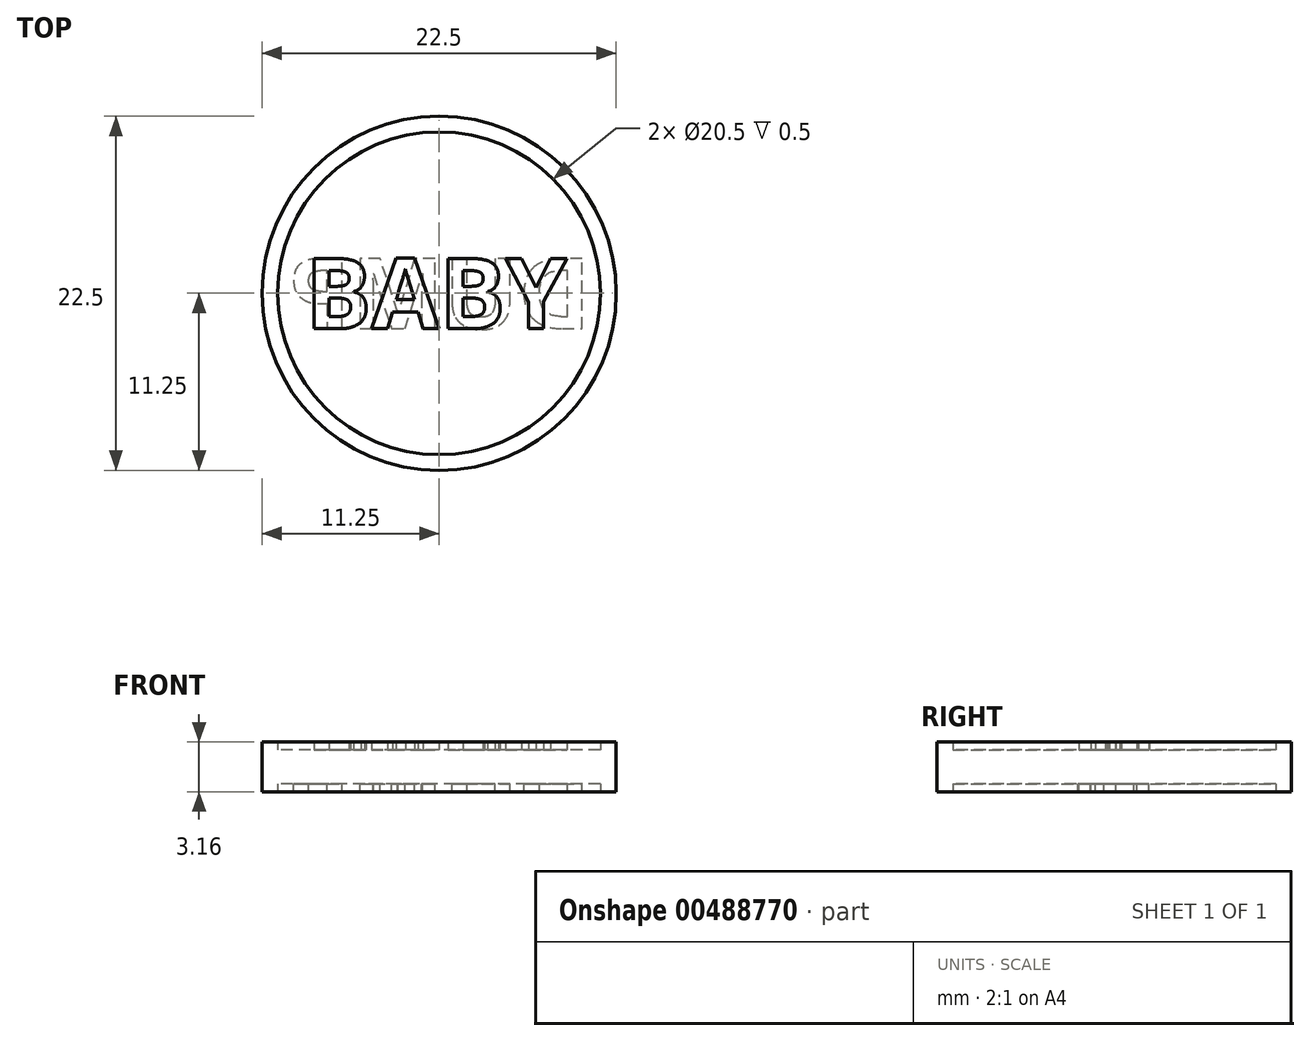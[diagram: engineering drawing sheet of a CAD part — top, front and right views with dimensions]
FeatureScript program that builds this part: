
annotation { "Feature Type Name" : "Feature", "Feature Type Description" : "" }
export const myFeature = defineFeature(function(context is Context, id is Id, definition is map)
    precondition{}
    {
        {
            var Q0;
            Q0=qCreatedBy(makeId("Top.planeOp"),FACE);
            var sketch = newSketch(context, id + "F0", { "sketchPlane" : qUnion([Q0])});
            skCircle(sketch, "E0", {"center": v(0, 0) * mm, "radius": 11.25 * mm});
            skCircle(sketch, "E1", {"center": v(0, 0) * mm, "radius": 10.25 * mm});
            skSolve(sketch);
        }
        {
            var Q0;
            Q0=makeQuery(id+"F0.imprint","IMPRINT",FACE,{"disambiguationData":[TD([[makeQuery(id+"F0.imprint","IMPRINT",EDGE,{"derivedFrom":sQuery(id+"F0.wireOp",EDGE,"E0")}),1.0]])]});
            extrude(context, id + "F1", {"entities" : qUnion([Q0]), "endBound" : BoundingType.SYMMETRIC, "depth" : 3.15 * mm});
        }
        {
            var Q0;
            Q0=qCreatedBy(makeId("Top.planeOp"),FACE);
            var sketch = newSketch(context, id + "F2", { "sketchPlane" : qUnion([Q0])});
            skCircle(sketch, "E2", {"center": v(0, 0) * mm, "radius": 11 * mm});
            skSolve(sketch);
        }
        {
            var Q0;
            Q0 = qSketchRegion(id + "F2", true);
            extrude(context, id + "F3", {"entities" : qUnion([Q0]), "operationType" : NewBodyOperationType.ADD, "endBound" : BoundingType.SYMMETRIC, "depth" : 2.15 * mm});
        }
        {
            var Q0;
            Q0=qCreatedBy(makeId("Top.planeOp"),FACE);
            var sketch = newSketch(context, id + "F4", { "sketchPlane" : qUnion([Q0])});
            skText(sketch, "E3", { "text": "BABY", "fontName": "OpenSans-Bold.ttf"});
            skPoint(sketch, "E4.endSnap0", {"position": v(8.5, 0) * mm});
            skLineSegment(sketch, "E5", {"start": v(-8.5, -2.25) * mm, "end": v(8.5, 2.25) * mm, "construction": true});
            const initialGuessF4  = {"E3": [-0.0085, -0.00225, 1, 0, 0.0045]};
            skSetInitialGuess(sketch, initialGuessF4);
            skSolve(sketch);
        }
        {
            var Q0;
            Q0 = qSketchRegion(id + "F4", true);
            var Q1;
            Q1=makeQuery(id+"F1.opExtrude","CAP_FACE",FACE,{"disambiguationData":[OSD([sQuery(id+"F0.wireOp",EDGE,"E0"),sQuery(id+"F0.wireOp",EDGE,"E1")])],"isStart":false});
            extrude(context, id + "F5", {"entities" : qUnion([Q0]), "operationType" : NewBodyOperationType.ADD, "endBound" : BoundingType.UP_TO_SURFACE, "endBoundEntityFace" : qUnion([Q1]), "depth" : .5 * mm});
        }
        {
            var Q0;
            Q0=makeQuery(id+"F3.opExtrude","CAP_FACE",FACE,{"disambiguationData":[OSD([sQuery(id+"F2.wireOp",EDGE,"E2")])],"isStart":true});
            var sketch = newSketch(context, id + "F6", { "sketchPlane" : qUnion([Q0])});
            skText(sketch, "E6", { "text": "DUMP", "fontName": "OpenSans-Bold.ttf"});
            skLineSegment(sketch, "E7", {"start": v(-9.65, -2.25) * mm, "end": v(9.65, 2.25) * mm, "construction": true});
            const initialGuessF6  = {"E6": [0.00965, 0.00225, -1, 0, 0.0045]};
            skSetInitialGuess(sketch, initialGuessF6);
            skSolve(sketch);
        }
        {
            var Q0;
            Q0 = qSketchRegion(id + "F6", true);
            var Q1;
            Q1=makeQuery(id+"F1.opExtrude","CAP_FACE",FACE,{"disambiguationData":[OSD([sQuery(id+"F0.wireOp",EDGE,"E0"),sQuery(id+"F0.wireOp",EDGE,"E1")])],"isStart":true});
            extrude(context, id + "F7", {"entities" : qUnion([Q0]), "operationType" : NewBodyOperationType.ADD, "endBound" : BoundingType.UP_TO_SURFACE, "endBoundEntityFace" : qUnion([Q1]), "depth" : 25 * mm});
        }
    });
